# Revit family: BuroSeating_Buro Metro II
name_source: partatom
category: Furniture
units: mm (PartAtom-declared; Revit-internal decimal feet)

## family parameters
Always vertical = Yes
Cut with Voids When Loaded = No
OmniClass Number = 23.40.70.14.64.11
OmniClass Title = Office Furniture
Room Calculation Point = No
Shared = Yes
Work Plane-Based = No

## types (4) — shared parameters
ArmRestMaterial = BuroSeating_Plastic_Black
ArmRestSupportMaterial = BuroSeating_Aluminium_Black
Assembly Code = E2020
BackFrameMaterial = BuroSeating_Plastic_Black
BackPanelMaterial = BuroSeating_Fabric_Mesh_Black
BackRestMaterial = BuroSeating_Fabric_Mesh_Black
BackSupportMaterial = BuroSeating_Aluminium_Black
BottomLiftMaterial = BuroSeating_Plastic_Black
CastorMaterial = BuroSeating_Aluminium_Black
CastorWheelMaterial = BuroSeating_Aluminium_Black
Description = Buro Metro II
FrameMaterial = BuroSeating_Aluminium_Black
Manufacturer = Buro Seating
NominalDepth = 630 mm
NominalHeight = 995 mm
NominalSeatDepthRange = 450-500
NominalSeatHeight = 470-600
NominalWidth = 610 mm
ProductGroup = Metro II
ProductPageURL AU = https://buroseating.com
ProductPageURL NZ = https://buroseating.co.nz
ProductRange = Buro
SeatDepth = 490 mm
SeatLeverFrameMaterial = BuroSeating_Aluminium_Black
SeatLeverHandleMaterial = BuroSeating_Aluminium_Black
SeatMaterial = BuroSeating_Fabric_Black
SeatSupportMaterial = BuroSeating_Aluminium_Black
SeatTiltMaterial = BuroSeating_Aluminium_Black
SeatWidth = 520 mm
TopLiftMaterial = BuroSeating_Aluminium_Black
Type Comments = Seat Height 470-600mm High
URL = https://buroseating.co.nz
URL AU = https://buroseating.com
WarrantyDescription = Full 5 year guarantee (excluding upholstery)
zero-valued in all types: Default Elevation

## per-type parameters (varying)
| type | BaseMaterial | Model | SeatArms |
| Buro Metro II Aluminium Base 222-153 | BuroSeating_Metal_Chrome_Semi-Polished | Buro Metro II Aluminium Base 222-153 | No |
| Buro Metro II Aluminium Base 222-153 w Arms | BuroSeating_Metal_Chrome_Semi-Polished | Buro Metro II Aluminium Base 222-153 with Arms | Yes |
| Buro Metro II Nylon Base 222-N-153 | BuroSeating_Plastic_Black | Buro Metro II Nylon Base 222-N-153 | No |
| Buro Metro II Nylon Base 222-N-153 w Arms | BuroSeating_Plastic_Black | Buro Metro II Nylon Base 222-N-153 with Arms | Yes |

## geometry (parser evidence)
native form markers: Sweep x13
no freeform markers — native parametric forms only
